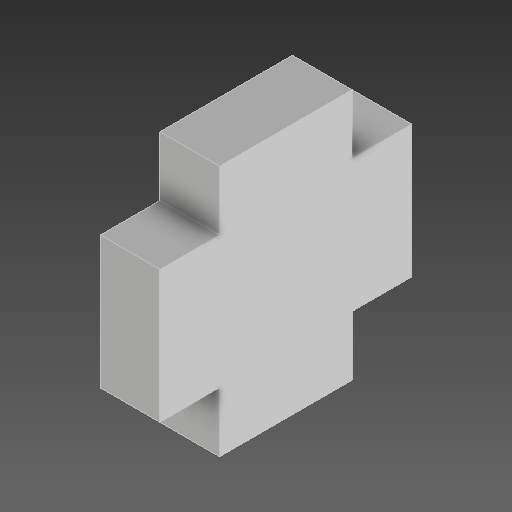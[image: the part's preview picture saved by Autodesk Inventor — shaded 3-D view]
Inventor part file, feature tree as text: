
AUTODESK INVENTOR PART (.ipt)
format: ipt  version: 2020.1 (Build 241239000, 239)  size: 127,488 bytes
history: native  units: mm
features: other x4, extrude x1, projected_geometry x1
ambient origin geometry x8: Origin, YZ Plane, XZ Plane, XY Plane, X Axis, Y Axis, Z Axis, Center Point
bodies: Solid1 (feature_tree)
feature tree (6):
  other  "Annotations"
  extrude  "Make Inner Rib by Extrusion of Its Profile"  Depth=20.0mm
  other  "Laser Cutter Sketch"
  other  "Inner Rib Profile"
  projected_geometry  "Projected Loop1"
  other  "General Note 1"
